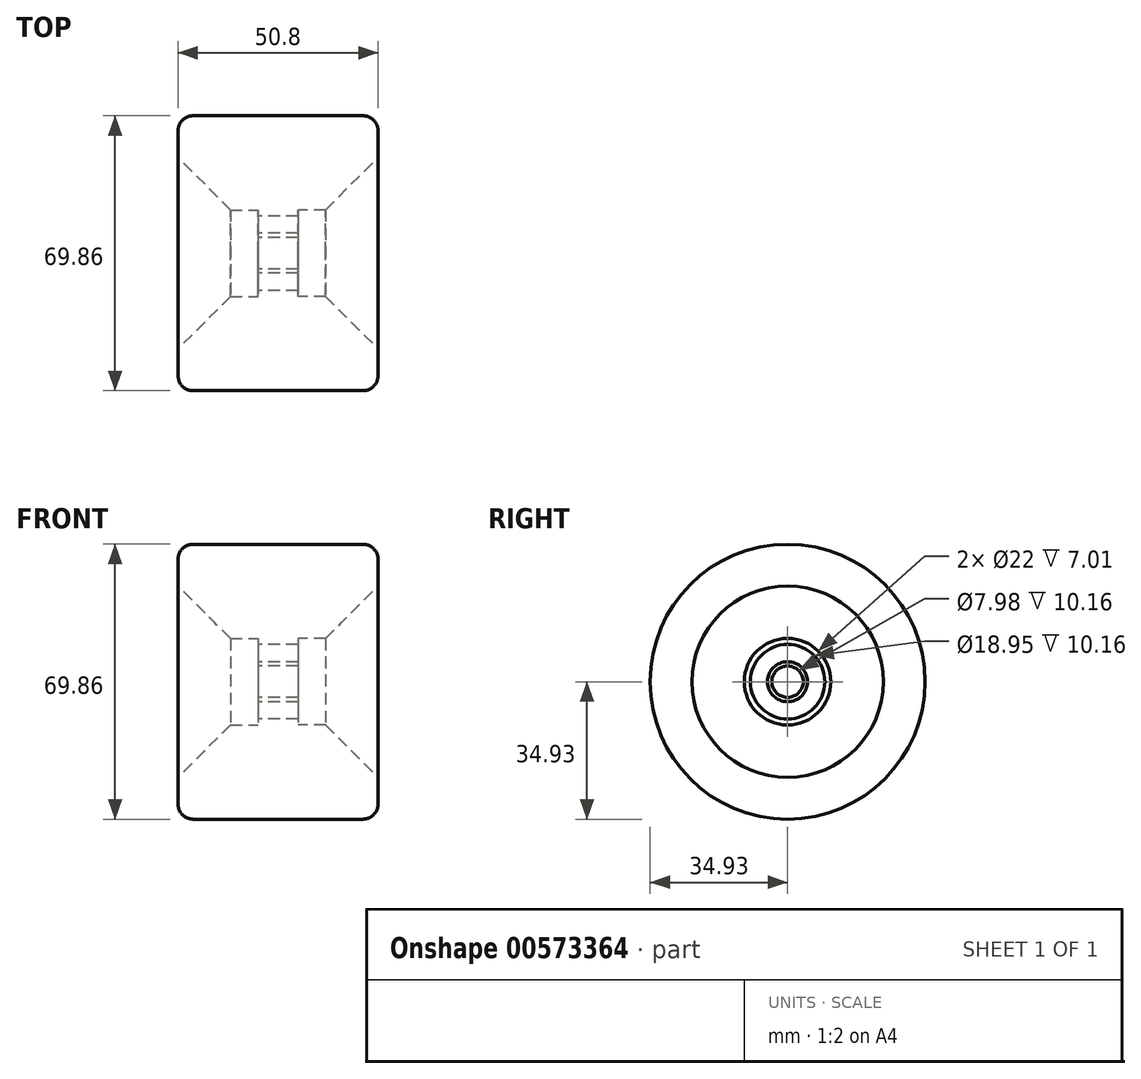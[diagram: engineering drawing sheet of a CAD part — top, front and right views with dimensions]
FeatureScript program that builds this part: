
annotation { "Feature Type Name" : "Feature", "Feature Type Description" : "" }
export const myFeature = defineFeature(function(context is Context, id is Id, definition is map)
    precondition{}
    {
        {
            var Q0;
            Q0=qCreatedBy(makeId("Front.planeOp"),FACE);
            var sketch = newSketch(context, id + "F0", { "sketchPlane" : qUnion([Q0])});
            skLineSegment(sketch, "E0.bottom", {"start": v(0, 34.93) * mm, "end": v(21.59, 34.92) * mm});
            skLineSegment(sketch, "E0.left", {"start": v(0, 34.92) * mm, "end": v(0, 9.47) * mm});
            skLineSegment(sketch, "E0.right", {"start": v(25.4, 31.12) * mm, "end": v(25.4, 24.3) * mm});
            skLineSegment(sketch, "E1.right", {"start": v(5.08, 11) * mm, "end": v(5.08, 9.47) * mm});
            skLineSegment(sketch, "E2", {"start": v(12.1, 11) * mm, "end": v(25.4, 24.3) * mm});
            skPoint(sketch, "E3.orphan", {"position": v(25.4, 13.7) * mm});
            skLineSegment(sketch, "E4", {"start": v(0, 0) * mm, "end": v(8.3, 0) * mm, "construction": true});
            skLineSegment(sketch, "E5", {"start": v(0, 9.47) * mm, "end": v(5.08, 9.47) * mm});
            skLineSegment(sketch, "E6", {"start": v(5.08, 11) * mm, "end": v(12.1, 11) * mm});
            skPoint(sketch, "E7.visualSharp", {"position": v(25.4, 34.92) * mm});
            skArc(sketch, "E7.filletArc", {"start": v(25.4, 31.12) * mm, "mid": v(24.28, 33.8) * mm, "end": v(21.59, 34.93) * mm});
            skLineSegment(sketch, "E8", {"start": v(0, 9.47) * mm, "end": v(0, 0) * mm, "construction": true});
            skSolve(sketch);
        }
        {
            var Q0;
            Q0 = qSketchRegion(id + "F0", true);
            var Q1;
            Q1=sQuery(id+"F0.wireOp",EDGE,"E4");
            revolve(context, id + "F1", {"entities" : qUnion([Q0]), "axis" : qUnion([Q1]), "revolveType" : RevolveType.FULL});
        }
        {
            var Q0;
            Q0=makeQuery(id+"F1.opRevolve","SWEPT_BODY",BODY,{"disambiguationData":[OSD([sQuery(id+"F0.wireOp",EDGE,"E0.bottom"),sQuery(id+"F0.wireOp",EDGE,"E0.left"),sQuery(id+"F0.wireOp",EDGE,"E0.right"),sQuery(id+"F0.wireOp",EDGE,"E1.right"),sQuery(id+"F0.wireOp",EDGE,"E2"),sQuery(id+"F0.wireOp",EDGE,"E5"),sQuery(id+"F0.wireOp",EDGE,"E6"),sQuery(id+"F0.wireOp",EDGE,"E7.filletArc")])]});
            var Q1;
            Q1=makeQuery(id+"F1.opRevolve","SWEPT_FACE",FACE,{"disambiguationData":[OSD([sQuery(id+"F0.wireOp",EDGE,"E0.left")])]});
            mirror(context, id + "F2", {"operationType" : NewBodyOperationType.ADD, "entities" : qUnion([Q0]), "mirrorPlane" : qUnion([Q1])});
        }
        {
            var Q0;
            Q0=qCreatedBy(makeId("Front.planeOp"),FACE);
            var sketch = newSketch(context, id + "F3", { "sketchPlane" : qUnion([Q0])});
            skLineSegment(sketch, "E9.bottom", {"start": v(-5.08, 5.08) * mm, "end": v(5.08, 5.08) * mm});
            skLineSegment(sketch, "E9.top", {"start": v(-5.08, 3.99) * mm, "end": v(5.08, 3.99) * mm});
            skLineSegment(sketch, "E9.left", {"start": v(-5.08, 5.08) * mm, "end": v(-5.08, 3.99) * mm});
            skLineSegment(sketch, "E9.right", {"start": v(5.08, 5.08) * mm, "end": v(5.08, 3.99) * mm});
            skLineSegment(sketch, "E10.0", {"start": v(0, 0) * mm, "end": v(8.3, 0) * mm, "construction": true});
            skSolve(sketch);
        }
        {
            var Q0;
            Q0 = qSketchRegion(id + "F3", true);
            var Q1;
            Q1=sQuery(id+"F3.wireOp",EDGE,"E10.0");
            revolve(context, id + "F4", {"entities" : qUnion([Q0]), "axis" : qUnion([Q1]), "revolveType" : RevolveType.FULL});
        }
    });
